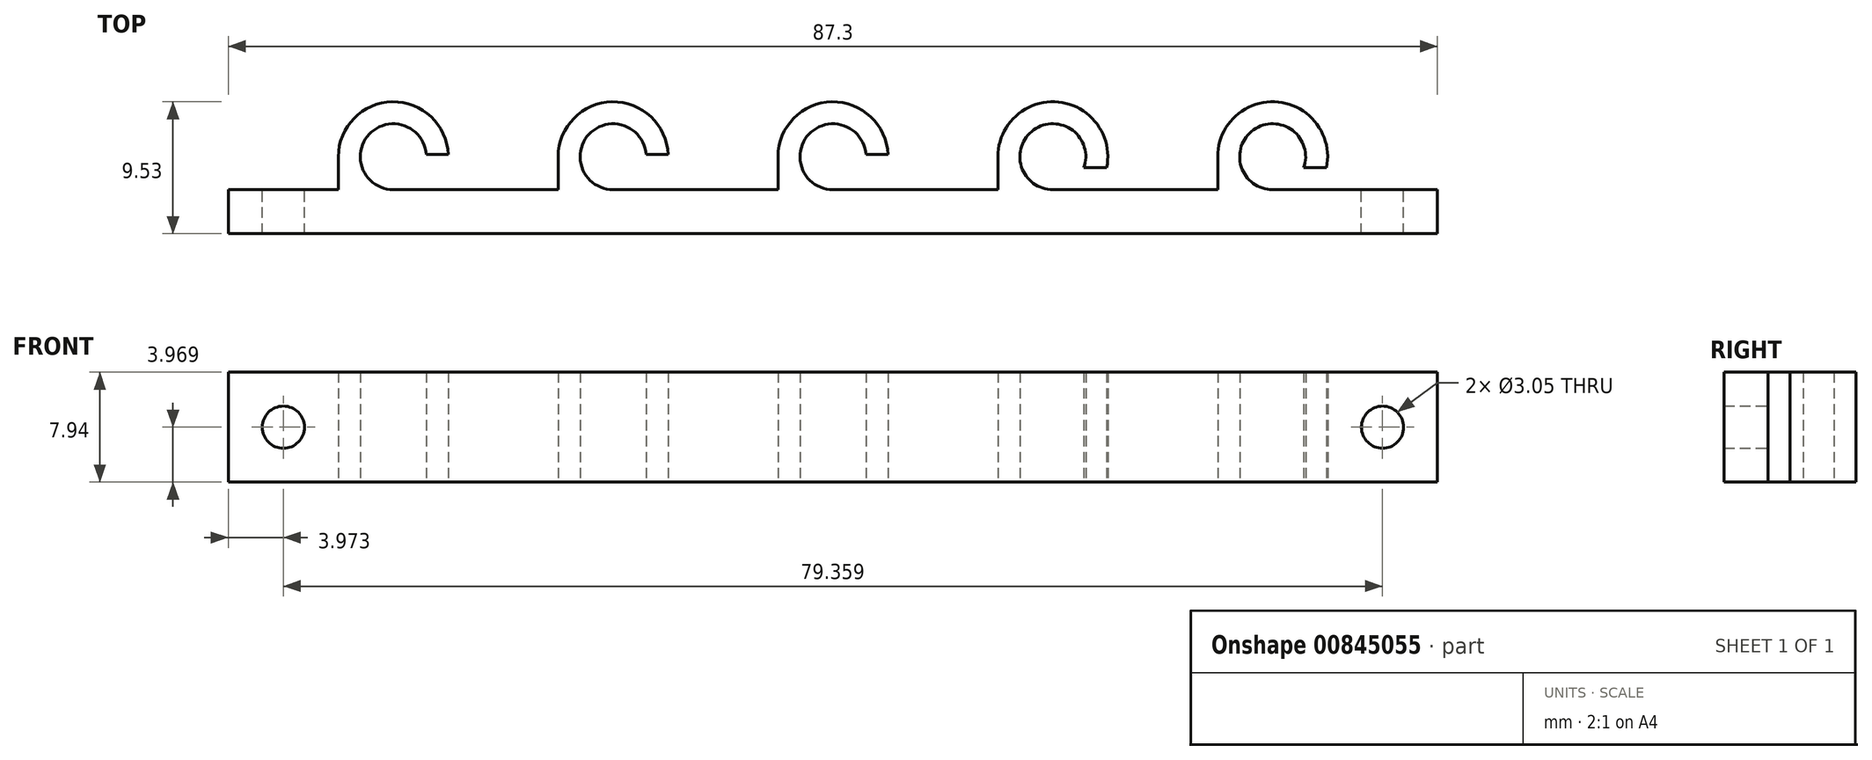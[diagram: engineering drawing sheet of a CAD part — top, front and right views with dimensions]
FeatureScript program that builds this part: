
annotation { "Feature Type Name" : "Feature", "Feature Type Description" : "" }
export const myFeature = defineFeature(function(context is Context, id is Id, definition is map)
    precondition{}
    {
        {
            var Q0;
            Q0=qCreatedBy(makeId("Top.planeOp"),FACE);
            var sketch = newSketch(context, id + "F0", { "sketchPlane" : qUnion([Q0])});
            skArc(sketch, "E0", {"start": v(2.38, 0.16) * mm, "mid": v(-1.74, 1.63) * mm, "end": v(0, -2.38) * mm});
            skArc(sketch, "E1", {"start": v(3.97, 0.16) * mm, "mid": v(-0.08, 3.97) * mm, "end": v(-3.97, 0) * mm});
            skLineSegment(sketch, "E2.top", {"start": v(-11.9, -5.56) * mm, "end": v(75.4, -5.56) * mm});
            skLineSegment(sketch, "E2.right", {"start": v(75.4, -2.38) * mm, "end": v(75.4, -5.56) * mm});
            skLineSegment(sketch, "E3", {"start": v(-3.97, 0) * mm, "end": v(-3.97, -2.38) * mm});
            skLineSegment(sketch, "E4.trimOffspring", {"start": v(67.45, -2.38) * mm, "end": v(75.4, -2.38) * mm});
            skLineSegment(sketch, "E5", {"start": v(2.38, 0.16) * mm, "end": v(3.97, 0.16) * mm});
            skLineSegment(sketch, "E6", {"start": v(0, -2.38) * mm, "end": v(3.97, -2.38) * mm});
            skPoint(sketch, "E7.orphan", {"position": v(3.97, 0) * mm});
            skLineSegment(sketch, "E8.1.0.0", {"start": v(11.9, 0) * mm, "end": v(11.9, -2.38) * mm});
            skLineSegment(sketch, "E8.1.0.1", {"start": v(18.25, 0.16) * mm, "end": v(19.84, 0.16) * mm});
            skArc(sketch, "E8.1.0.3", {"start": v(19.84, 0.16) * mm, "mid": v(15.8, 3.97) * mm, "end": v(11.9, 0) * mm});
            skArc(sketch, "E8.1.0.4", {"start": v(18.25, 0.16) * mm, "mid": v(14.13, 1.63) * mm, "end": v(15.87, -2.38) * mm});
            skLineSegment(sketch, "E8.1.0.5", {"start": v(15.87, -2.38) * mm, "end": v(19.84, -2.38) * mm});
            skLineSegment(sketch, "E8.2.0.0", {"start": v(27.77, 0) * mm, "end": v(27.77, -2.38) * mm});
            skLineSegment(sketch, "E8.2.0.1", {"start": v(34.12, 0.16) * mm, "end": v(35.7, 0.16) * mm});
            skArc(sketch, "E8.2.0.3", {"start": v(35.7, 0.16) * mm, "mid": v(31.66, 3.97) * mm, "end": v(27.77, 0) * mm});
            skArc(sketch, "E8.2.0.4", {"start": v(34.12, 0.16) * mm, "mid": v(30, 1.63) * mm, "end": v(31.74, -2.38) * mm});
            skLineSegment(sketch, "E8.2.0.5", {"start": v(31.74, -2.38) * mm, "end": v(35.7, -2.38) * mm});
            skLineSegment(sketch, "E8.3.0.0", {"start": v(43.65, 0) * mm, "end": v(43.65, -2.38) * mm});
            skLineSegment(sketch, "E8.3.0.1", {"start": v(49.86, -0.8) * mm, "end": v(51.5, -0.8) * mm});
            skArc(sketch, "E8.3.0.3", {"start": v(51.5, -0.8) * mm, "mid": v(48.01, 3.95) * mm, "end": v(43.65, 0) * mm});
            skArc(sketch, "E8.3.0.4", {"start": v(49.86, -0.8) * mm, "mid": v(46.24, 1.94) * mm, "end": v(47.62, -2.38) * mm});
            skLineSegment(sketch, "E8.3.0.5", {"start": v(47.62, -2.38) * mm, "end": v(51.58, -2.38) * mm});
            skLineSegment(sketch, "E8.4.0.0", {"start": v(59.52, 0) * mm, "end": v(59.52, -2.38) * mm});
            skLineSegment(sketch, "E8.4.0.1", {"start": v(65.73, -0.8) * mm, "end": v(67.38, -0.8) * mm});
            skArc(sketch, "E8.4.0.3", {"start": v(67.38, -0.8) * mm, "mid": v(63.89, 3.95) * mm, "end": v(59.52, 0) * mm});
            skArc(sketch, "E8.4.0.4", {"start": v(65.73, -0.8) * mm, "mid": v(62.11, 1.94) * mm, "end": v(63.49, -2.38) * mm});
            skLineSegment(sketch, "E8.4.0.5", {"start": v(63.49, -2.38) * mm, "end": v(67.45, -2.38) * mm});
            skLineSegment(sketch, "E9", {"start": v(-11.9, -5.56) * mm, "end": v(-11.9, -2.38) * mm});
            skLineSegment(sketch, "E10", {"start": v(-11.9, -2.38) * mm, "end": v(-3.97, -2.38) * mm});
            skPoint(sketch, "E2.left.start.orphan", {"position": v(-75.4, -2.38) * mm});
            skLineSegment(sketch, "E11", {"start": v(3.97, -2.38) * mm, "end": v(11.9, -2.38) * mm});
            skLineSegment(sketch, "E12", {"start": v(19.84, -2.38) * mm, "end": v(27.77, -2.38) * mm});
            skLineSegment(sketch, "E13", {"start": v(35.7, -2.38) * mm, "end": v(43.65, -2.38) * mm});
            skLineSegment(sketch, "E14", {"start": v(51.58, -2.38) * mm, "end": v(59.52, -2.38) * mm});
            skSolve(sketch);
        }
        {
            var Q0;
            Q0 = qSketchRegion(id + "F0", true);
            extrude(context, id + "F1", {"entities" : qUnion([Q0]), "depth" : 7.94 * mm, "offsetDistance" : 25.4 * mm});
        }
        {
            var Q0;
            Q0=makeQuery(id+"F1.opExtrude","SWEPT_FACE",FACE,{"disambiguationData":[OSD([sQuery(id+"F0.wireOp",EDGE,"E10")])]});
            var sketch = newSketch(context, id + "F2", { "sketchPlane" : qUnion([Q0])});
            skCircle(sketch, "E15", {"center": v(7.94, 3.97) * mm, "radius": 1.52 * mm});
            skCircle(sketch, "E16", {"center": v(-71.42, 3.97) * mm, "radius": 1.52 * mm});
            skLineSegment(sketch, "E17", {"start": v(11.9, 3.97) * mm, "end": v(7.94, 3.97) * mm, "construction": true});
            skLineSegment(sketch, "E18", {"start": v(7.94, 3.97) * mm, "end": v(7.94, 7.94) * mm, "construction": true});
            skPoint(sketch, "E18.endSnap0", {"position": v(7.94, 7.94) * mm});
            skLineSegment(sketch, "E19", {"start": v(-71.42, 3.97) * mm, "end": v(-75.4, 3.97) * mm, "construction": true});
            skSolve(sketch);
        }
        {
            var Q0;
            Q0 = qSketchRegion(id + "F2", true);
            extrude(context, id + "F3", {"entities" : qUnion([Q0]), "operationType" : NewBodyOperationType.REMOVE, "endBound" : BoundingType.THROUGH_ALL, "oppositeDirection" : true, "depth" : 25.4 * mm, "offsetDistance" : 25.4 * mm});
        }
    });
